# Revit family: SH-1011
name_source: partatom
category: Lighting Fixtures
revit_build: Autodesk Revit 2017 (Build: 20160225_1515(x64)
units: mm (PartAtom-declared; Revit-internal decimal feet)

## family parameters
Always vertical = Yes
Cut with Voids When Loaded = No
Light Source = No
OmniClass Number = 23.80.70.00
OmniClass Title = Lighting
Part Type = Normal
Room Calculation Point = No
Round Connector Dimension = Use Diameter
Shared = No
Work Plane-Based = No

## types (1)
- SH-1011(Aluminium body-3000K-LED)
    Body Material = Aluminium
    Body color = Black
    Diameter = 7.2 cm
    Flicker = FREE Flicker
    Height = 11.2 cm
    IP = IP65
    Lamp = LED
    Manufacturer = SHOA
    Model = SH-1011
    Protection Class = class I
    Type medule = Power Led
    URL = https://www.shoaco.com
    Voltage/Frequency = 230V-50HZ
    color rendering index(CRI) = 80
    color temperature = 3000K
    consumption current = 0 A
    cutout Depth = 9.5 cm
    instalation = inground
    wattage. = 1 W
    website = www.shoaco.com

## geometry (parser evidence)
native form markers: Sweep x3
no freeform markers — native parametric forms only
